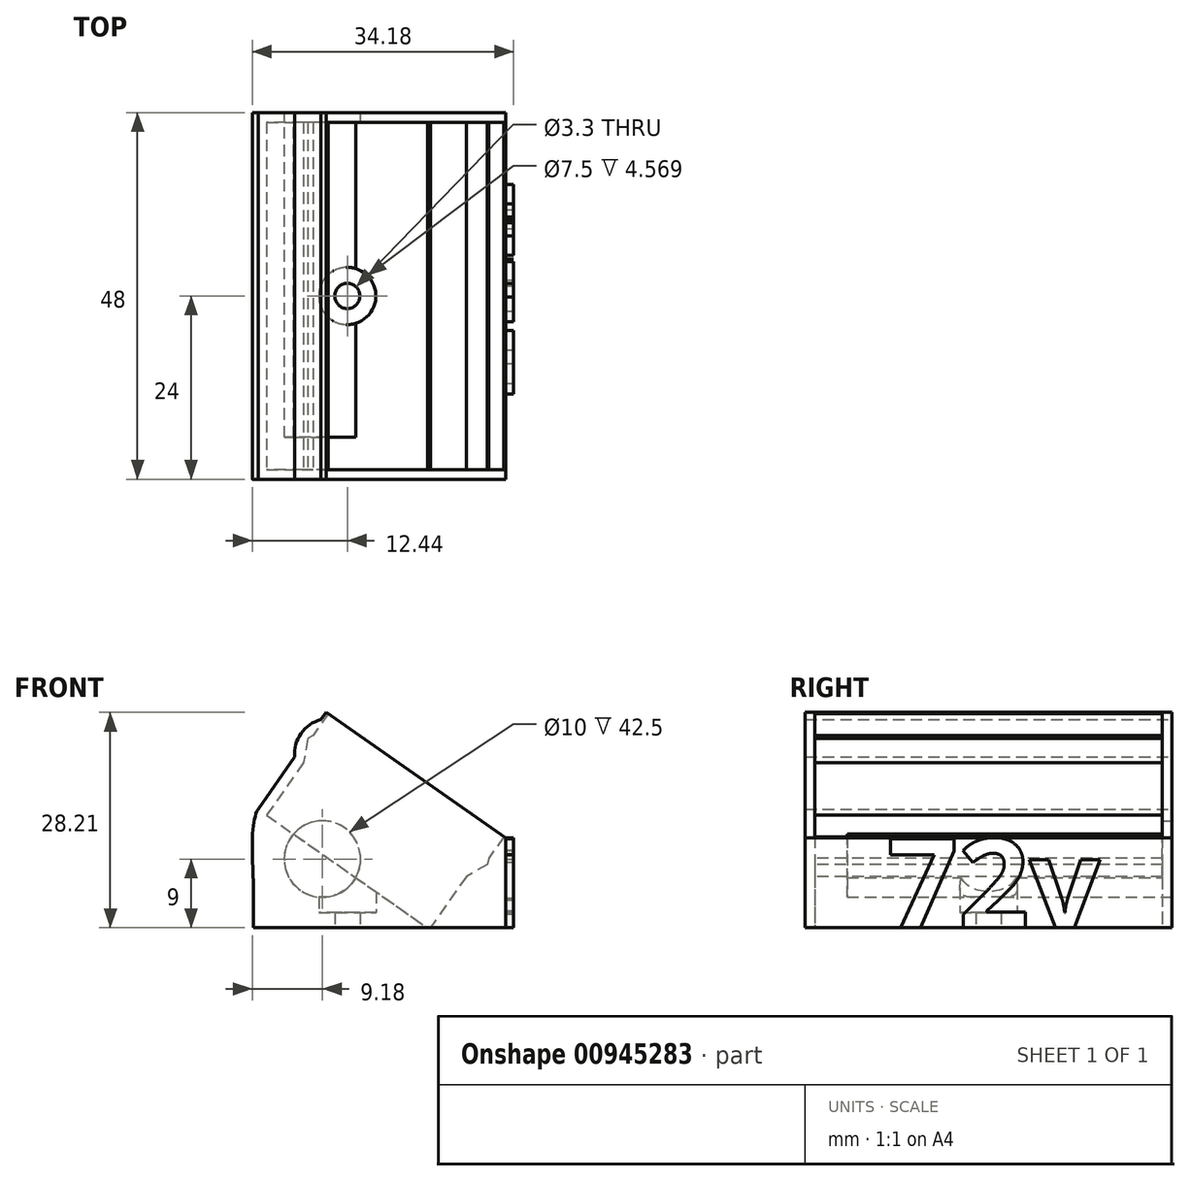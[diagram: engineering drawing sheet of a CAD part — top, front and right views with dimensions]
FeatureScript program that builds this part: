
annotation { "Feature Type Name" : "Feature", "Feature Type Description" : "" }
export const myFeature = defineFeature(function(context is Context, id is Id, definition is map)
    precondition{}
    {
        {
            var Q0;
            Q0=qCreatedBy(makeId("Front.planeOp"),FACE);
            var sketch = newSketch(context, id + "F0", { "sketchPlane" : qUnion([Q0])});
            skLineSegment(sketch, "E0.bottom", {"start": v(0, 0) * mm, "end": v(-33, 0) * mm});
            skLineSegment(sketch, "E0.top", {"start": v(0, 4) * mm, "end": v(-33, 4) * mm});
            skLineSegment(sketch, "E0.left", {"start": v(0, 0) * mm, "end": v(0, 4) * mm});
            skLineSegment(sketch, "E0.right", {"start": v(-33, 0) * mm, "end": v(-33, 4) * mm});
            skLineSegment(sketch, "E1", {"start": v(-30.88, 15.06) * mm, "end": v(-9.83, 0.32) * mm, "construction": true});
            skLineSegment(sketch, "E2", {"start": v(-9.83, 0.32) * mm, "end": v(-1.23, 12.6) * mm, "construction": true});
            skLineSegment(sketch, "E3", {"start": v(-1.23, 12.6) * mm, "end": v(0, 11.74) * mm, "construction": true});
            skLineSegment(sketch, "E4", {"start": v(-22.28, 27.35) * mm, "end": v(-30.88, 15.06) * mm, "construction": true});
            skLineSegment(sketch, "E5", {"start": v(0, 4) * mm, "end": v(0, 11.74) * mm});
            skLineSegment(sketch, "E6", {"start": v(-32.4, 15.5) * mm, "end": v(-15.96, 4) * mm});
            skLineSegment(sketch, "E7", {"start": v(0, 7.87) * mm, "end": v(13.32, 7.87) * mm});
            skLineSegment(sketch, "E8", {"start": v(13.32, 7.87) * mm, "end": v(13.32, 0) * mm});
            skLineSegment(sketch, "E9", {"start": v(13.32, 0) * mm, "end": v(0, 0) * mm});
            skLineSegment(sketch, "E10", {"start": v(21.82, 30.5) * mm, "end": v(-34.66, 30.5) * mm, "construction": true});
            skLineSegment(sketch, "E11", {"start": v(-22.28, 27.35) * mm, "end": v(-23.5, 28.2) * mm, "construction": true});
            skLineSegment(sketch, "E12", {"start": v(-23.5, 28.2) * mm, "end": v(-21.9, 30.5) * mm, "construction": true});
            skLineSegment(sketch, "E13", {"start": v(-21.9, 30.5) * mm, "end": v(1.6, 14.04) * mm, "construction": true});
            skLineSegment(sketch, "E14", {"start": v(0, 11.74) * mm, "end": v(1.6, 14.04) * mm, "construction": true});
            skLineSegment(sketch, "E15", {"start": v(-29.2, 13.88) * mm, "end": v(-31.73, 10.28) * mm, "construction": true});
            skLineSegment(sketch, "E16", {"start": v(-31.73, 10.28) * mm, "end": v(-14.04, -2.11) * mm, "construction": true});
            skLineSegment(sketch, "E17", {"start": v(-14.04, -2.11) * mm, "end": v(-11.51, 1.5) * mm, "construction": true});
            skLineSegment(sketch, "E18", {"start": v(-22.88, 4.08) * mm, "end": v(-20.36, 7.69) * mm, "construction": true});
            skLineSegment(sketch, "E19", {"start": v(0, 11.74) * mm, "end": v(-23.5, 28.2) * mm});
            skLineSegment(sketch, "E20", {"start": v(-23.5, 28.2) * mm, "end": v(-32.4, 15.5) * mm});
            skLineSegment(sketch, "E21", {"start": v(-1.1, 12.52) * mm, "end": v(-9.87, 0) * mm});
            skLineSegment(sketch, "E22", {"start": v(-22.4, 27.43) * mm, "end": v(-31.3, 14.74) * mm});
            skFitSpline(sketch, "E23", {"points": [v(-32.4, 15.5) * mm, v(-33, 4) * mm], "startDerivative": vector(-3.84, -5.87) * mm, "endDerivative": vector(0, -11.95) * mm});
            skLineSegment(sketch, "E24", {"start": v(-15.96, 4) * mm, "end": v(-10.25, 0) * mm});
            skLineSegment(sketch, "E25", {"start": v(-23.03, 26.54) * mm, "end": v(-25.92, 24.77) * mm});
            skLineSegment(sketch, "E26", {"start": v(-25.92, 24.77) * mm, "end": v(-26.47, 21.62) * mm});
            skLineSegment(sketch, "E27.MirrorCS", {"start": v(-1.73, 11.62) * mm, "end": v(-2.4, 8.3) * mm});
            skLineSegment(sketch, "E28.MirrorCS", {"start": v(-2.4, 8.3) * mm, "end": v(-5.17, 6.7) * mm});
            skArc(sketch, "E29", {"start": v(-24.18, 27.25) * mm, "mid": v(-26.8, 25.44) * mm, "end": v(-27.6, 22.35) * mm});
            skLineSegment(sketch, "E30", {"start": v(-23.25, 28.02) * mm, "end": v(-25.23, 25.19) * mm});
            skLineSegment(sketch, "E31.MirrorCS", {"start": v(-0.26, 11.93) * mm, "end": v(-2.25, 9.1) * mm});
            skSolve(sketch);
        }
        {
            var Q0;
            {var subQ0=sQuery(id+"F0.wireOp",EDGE,"E29");Q0=makeQuery(id+"F0.imprint","IMPRINT",FACE,{"disambiguationData":[TD([[makeQuery(id+"F0.imprint","IMPRINT",EDGE,{"derivedFrom":subQ0}),1.0]])]});}
            var Q1;
            {var subQ0=sQuery(id+"F0.wireOp",EDGE,"E23");Q1=makeQuery(id+"F0.imprint","IMPRINT",FACE,{"disambiguationData":[TD([[makeQuery(id+"F0.imprint","IMPRINT",EDGE,{"derivedFrom":subQ0}),1.0]])]});}
            var Q2;
            {var subQ0=sQuery(id+"F0.wireOp",EDGE,"E0.right");Q2=makeQuery(id+"F0.imprint","IMPRINT",FACE,{"disambiguationData":[TD([[makeQuery(id+"F0.imprint","IMPRINT",EDGE,{"derivedFrom":subQ0}),-1.0]])]});}
            var Q3;
            {var subQ0=sQuery(id+"F0.wireOp",EDGE,"E0.left");Q3=makeQuery(id+"F0.imprint","IMPRINT",FACE,{"disambiguationData":[TD([[makeQuery(id+"F0.imprint","IMPRINT",EDGE,{"derivedFrom":subQ0}),1.0]])]});}
            var Q4;
            {var subQ9=sQuery(id+"F0.wireOp",EDGE,"E27.MirrorCS");Q4=makeQuery(id+"F0.imprint","IMPRINT",FACE,{"disambiguationData":[TD([[makeQuery(id+"F0.imprint","IMPRINT",EDGE,{"derivedFrom":subQ9}),1.0]])]});}
            var Q5;
            {var subQ0=sQuery(id+"F0.wireOp",EDGE,"E21");var subQ1=sQuery(id+"F0.wireOp",EDGE,"E19");var subQ2=makeQuery(id+"F0.imprint","INTERSECT",VERTEX,{"derivedFrom":[subQ1,subQ0]});Q5=makeQuery(id+"F0.imprint","IMPRINT",FACE,{"disambiguationData":[TD([[makeQuery(id+"F0.imprint","IMPRINT",EDGE,{"disambiguationData":[TD([[subQ2,-1.0]])],"derivedFrom":subQ1}),1.0]])]});}
            var Q6;
            {var subQ0=sQuery(id+"F0.wireOp",EDGE,"E27.MirrorCS");Q6=makeQuery(id+"F0.imprint","IMPRINT",FACE,{"disambiguationData":[TD([[makeQuery(id+"F0.imprint","IMPRINT",EDGE,{"derivedFrom":subQ0}),-1.0]])]});}
            var Q7;
            {var subQ3=sQuery(id+"F0.wireOp",EDGE,"E24");Q7=makeQuery(id+"F0.imprint","IMPRINT",FACE,{"disambiguationData":[TD([[makeQuery(id+"F0.imprint","IMPRINT",EDGE,{"derivedFrom":subQ3}),1.0]])]});}
            var Q8;
            {var subQ0=sQuery(id+"F0.wireOp",EDGE,"E25");Q8=makeQuery(id+"F0.imprint","IMPRINT",FACE,{"disambiguationData":[TD([[makeQuery(id+"F0.imprint","IMPRINT",EDGE,{"derivedFrom":subQ0}),1.0]])]});}
            var Q9;
            {var subQ4=sQuery(id+"F0.wireOp",EDGE,"E26");Q9=makeQuery(id+"F0.imprint","IMPRINT",FACE,{"disambiguationData":[TD([[makeQuery(id+"F0.imprint","IMPRINT",EDGE,{"derivedFrom":subQ4}),-1.0]])]});}
            var Q10;
            {var subQ6=sQuery(id+"F0.wireOp",EDGE,"E30");Q10=makeQuery(id+"F0.imprint","IMPRINT",FACE,{"disambiguationData":[TD([[makeQuery(id+"F0.imprint","IMPRINT",EDGE,{"derivedFrom":subQ6}),-1.0]])]});}
            var Q11;
            {var subQ3=sQuery(id+"F0.wireOp",EDGE,"E30");Q11=makeQuery(id+"F0.imprint","IMPRINT",FACE,{"disambiguationData":[TD([[makeQuery(id+"F0.imprint","IMPRINT",EDGE,{"derivedFrom":subQ3}),1.0]])]});}
            var Q12;
            {var subQ4=sQuery(id+"F0.wireOp",EDGE,"E28.MirrorCS");Q12=makeQuery(id+"F0.imprint","IMPRINT",FACE,{"disambiguationData":[TD([[makeQuery(id+"F0.imprint","IMPRINT",EDGE,{"derivedFrom":subQ4}),1.0]])]});}
            extrude(context, id + "F1", {"entities" : qUnion([Q0, Q1, Q2, Q3, Q4, Q5, Q6, Q7, Q8, Q9, Q10, Q11, Q12]), "endBound" : BoundingType.SYMMETRIC, "depth" : 48 * mm, "offsetDistance" : 25 * mm});
        }
        {
            var Q0;
            {var subQ0=sQuery(id+"F0.wireOp",EDGE,"E21");var subQ1=sQuery(id+"F0.wireOp",EDGE,"E19");var subQ2=makeQuery(id+"F0.imprint","INTERSECT",VERTEX,{"derivedFrom":[subQ1,subQ0]});Q0=makeQuery(id+"F0.imprint","IMPRINT",FACE,{"disambiguationData":[TD([[makeQuery(id+"F0.imprint","IMPRINT",EDGE,{"disambiguationData":[TD([[subQ2,-1.0]])],"derivedFrom":subQ1}),1.0]])]});}
            var Q1;
            {var subQ0=sQuery(id+"F0.wireOp",EDGE,"E25");Q1=makeQuery(id+"F0.imprint","IMPRINT",FACE,{"disambiguationData":[TD([[makeQuery(id+"F0.imprint","IMPRINT",EDGE,{"derivedFrom":subQ0}),1.0]])]});}
            var Q2;
            {var subQ0=sQuery(id+"F0.wireOp",EDGE,"E27.MirrorCS");Q2=makeQuery(id+"F0.imprint","IMPRINT",FACE,{"disambiguationData":[TD([[makeQuery(id+"F0.imprint","IMPRINT",EDGE,{"derivedFrom":subQ0}),-1.0]])]});}
            var Q3;
            {var subQ3=sQuery(id+"F0.wireOp",EDGE,"E24");Q3=makeQuery(id+"F0.imprint","IMPRINT",FACE,{"disambiguationData":[TD([[makeQuery(id+"F0.imprint","IMPRINT",EDGE,{"derivedFrom":subQ3}),1.0]])]});}
            var Q4;
            {var subQ3=sQuery(id+"F0.wireOp",EDGE,"E30");Q4=makeQuery(id+"F0.imprint","IMPRINT",FACE,{"disambiguationData":[TD([[makeQuery(id+"F0.imprint","IMPRINT",EDGE,{"derivedFrom":subQ3}),1.0]])]});}
            var Q5;
            {var subQ3=sQuery(id+"F0.wireOp",EDGE,"E31.MirrorCS");Q5=makeQuery(id+"F0.imprint","IMPRINT",FACE,{"disambiguationData":[TD([[makeQuery(id+"F0.imprint","IMPRINT",EDGE,{"derivedFrom":subQ3}),-1.0]])]});}
            extrude(context, id + "F2", {"entities" : qUnion([Q0, Q1, Q2, Q3, Q4, Q5]), "operationType" : NewBodyOperationType.REMOVE, "endBound" : BoundingType.SYMMETRIC, "oppositeDirection" : true, "depth" : 45.5 * mm, "offsetDistance" : 25 * mm});
        }
        {
            var Q0;
            Q0=makeQuery(id+"F1.opExtrude","CAP_FACE",FACE,{"disambiguationData":[OSD([sQuery(id+"F0.wireOp",EDGE,"E0.bottom"),sQuery(id+"F0.wireOp",EDGE,"E0.left"),sQuery(id+"F0.wireOp",EDGE,"E0.right"),sQuery(id+"F0.wireOp",EDGE,"E5"),sQuery(id+"F0.wireOp",EDGE,"E19"),sQuery(id+"F0.wireOp",EDGE,"E20"),sQuery(id+"F0.wireOp",EDGE,"E23"),sQuery(id+"F0.wireOp",EDGE,"E29")])],"isStart":true});
            var sketch = newSketch(context, id + "F3", { "sketchPlane" : qUnion([Q0])});
            skCircle(sketch, "E32", {"center": v(24, 9) * mm, "radius": 5 * mm});
            skSolve(sketch);
        }
        {
            var Q0;
            Q0=makeQuery(id+"F3.imprint","IMPRINT",FACE,{"disambiguationData":[TD([[makeQuery(id+"F3.imprint","IMPRINT",EDGE,{"derivedFrom":sQuery(id+"F3.wireOp",EDGE,"E32")}),1.0]])]});
            extrude(context, id + "F4", {"entities" : qUnion([Q0]), "operationType" : NewBodyOperationType.REMOVE, "oppositeDirection" : true, "depth" : 42.5 * mm, "offsetDistance" : 25 * mm});
        }
        {
            var Q0;
            Q0=qCreatedBy(makeId("Top.planeOp"),FACE);
            var sketch = newSketch(context, id + "F5", { "sketchPlane" : qUnion([Q0])});
            skCircle(sketch, "E33", {"center": v(-20.74, 0) * mm, "radius": 1.65 * mm});
            skCircle(sketch, "E34", {"center": v(-20.74, 0) * mm, "radius": 3.75 * mm});
            skSolve(sketch);
        }
        {
            var Q0;
            Q0=makeQuery(id+"F5.imprint","IMPRINT",FACE,{"disambiguationData":[TD([[makeQuery(id+"F5.imprint","IMPRINT",EDGE,{"derivedFrom":sQuery(id+"F5.wireOp",EDGE,"E33")}),1.0]])]});
            var Q1;
            Q1=sQuery(id+"F5.wireOp",EDGE,"E33");
            extrude(context, id + "F6", {"entities" : qUnion([Q0]), "operationType" : NewBodyOperationType.REMOVE, "surfaceEntities" : qUnion([Q1]), "depth" : 25 * mm, "offsetDistance" : 25 * mm});
        }
        {
            var Q0;
            Q0=makeQuery(id+"F5.imprint","IMPRINT",FACE,{"disambiguationData":[TD([[makeQuery(id+"F5.imprint","IMPRINT",EDGE,{"derivedFrom":sQuery(id+"F5.wireOp",EDGE,"E33")}),-1.0]])]});
            extrude(context, id + "F7", {"entities" : qUnion([Q0]), "operationType" : NewBodyOperationType.REMOVE, "depth" : 25 * mm, "offsetDistance" : 25 * mm, "hasSecondDirection" : true, "secondDirectionOppositeDirection" : false, "secondDirectionDepth" : 2 * mm});
        }
        {
            var Q0;
            Q0=makeQuery(id+"F1.opExtrude","SWEPT_FACE",FACE,{"disambiguationData":[OSD([sQuery(id+"F0.wireOp",EDGE,"E0.left"),sQuery(id+"F0.wireOp",EDGE,"E5")])]});
            var sketch = newSketch(context, id + "F8", { "sketchPlane" : qUnion([Q0])});
            skText(sketch, "E35", { "text": "72v", "fontName": "OpenSans-Bold.ttf"});
            const initialGuessF8  = {"E35": [-0.01328, 0, 1, 0, 0.01174]};
            skSetInitialGuess(sketch, initialGuessF8);
            skSolve(sketch);
        }
        {
            var Q0;
            Q0=makeQuery(id+"F8.imprint","IMPRINT",FACE,{"disambiguationData":[TD([[makeQuery(id+"F8.imprint","IMPRINT",EDGE,{"derivedFrom":sQuery(id+"F8.wireOp",EDGE,"E35.sketch_text.stroke-0")}),-1.0]])]});
            var Q1;
            Q1=makeQuery(id+"F8.imprint","IMPRINT",FACE,{"disambiguationData":[TD([[makeQuery(id+"F8.imprint","IMPRINT",EDGE,{"derivedFrom":sQuery(id+"F8.wireOp",EDGE,"E35.sketch_text.stroke-7")}),1.0]])]});
            var Q2;
            Q2=makeQuery(id+"F8.imprint","IMPRINT",FACE,{"disambiguationData":[TD([[makeQuery(id+"F8.imprint","IMPRINT",EDGE,{"derivedFrom":sQuery(id+"F8.wireOp",EDGE,"E35.sketch_text.stroke-31")}),-1.0]])]});
            extrude(context, id + "F9", {"entities" : qUnion([Q0, Q1, Q2]), "operationType" : NewBodyOperationType.ADD, "depth" : 1 * mm, "offsetDistance" : 25 * mm});
        }
    });
